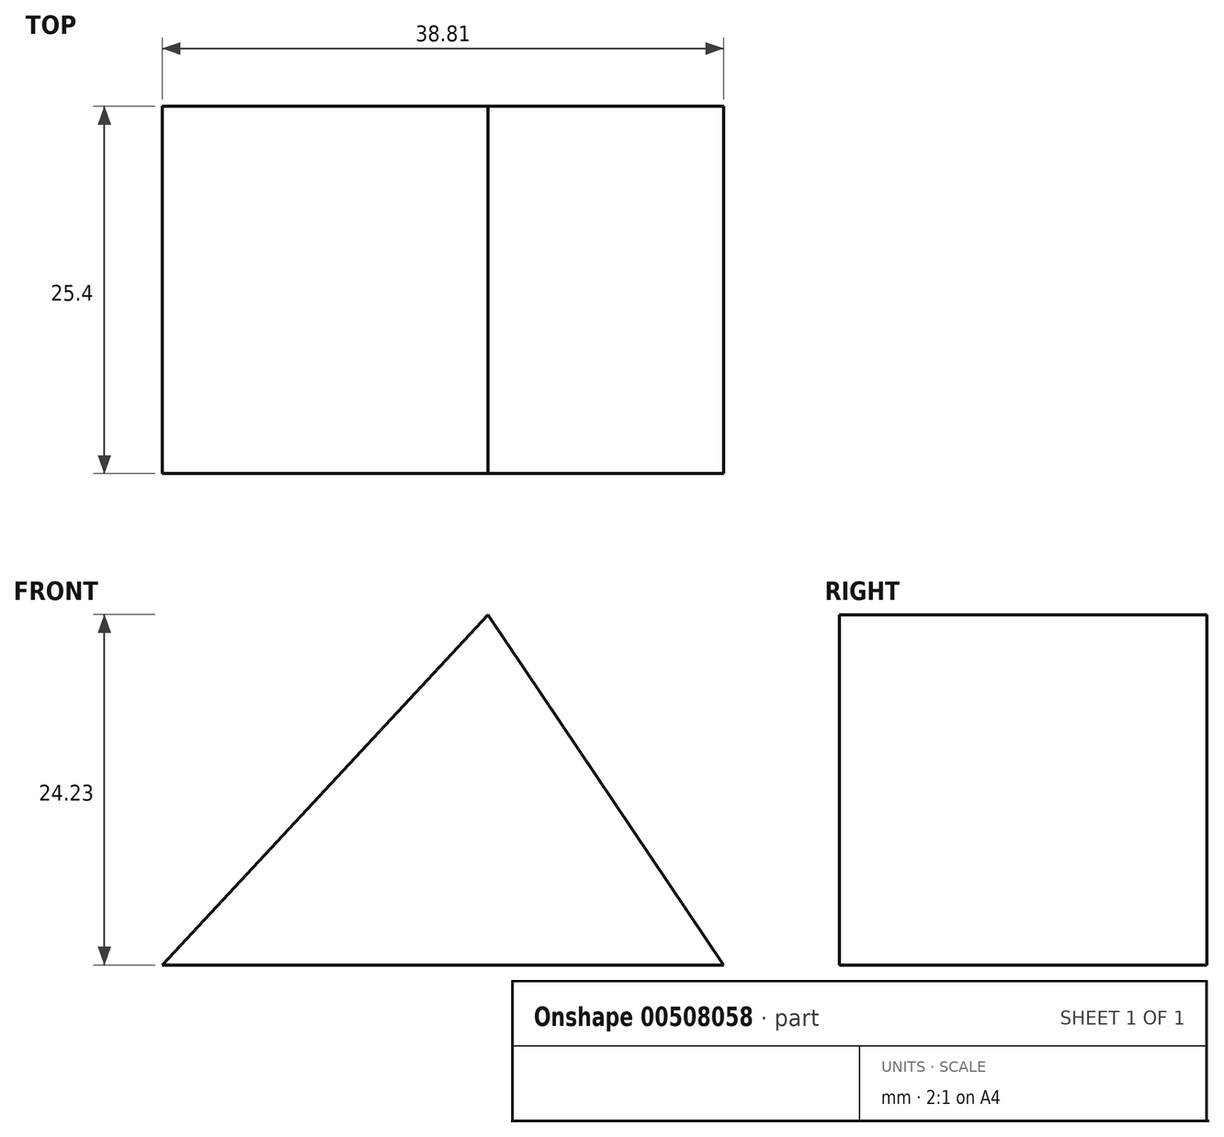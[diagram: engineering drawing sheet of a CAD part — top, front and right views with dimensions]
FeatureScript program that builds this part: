
annotation { "Feature Type Name" : "Feature", "Feature Type Description" : "" }
export const myFeature = defineFeature(function(context is Context, id is Id, definition is map)
    precondition{}
    {
        {
            var Q0;
            Q0=qCreatedBy(makeId("Front.planeOp"),FACE);
            var sketch = newSketch(context, id + "F0", { "sketchPlane" : qUnion([Q0])});
            skLineSegment(sketch, "E0", {"start": v(-45.56, 68.53) * mm, "end": v(-68.08, 44.3) * mm});
            skLineSegment(sketch, "E1", {"start": v(-68.08, 44.3) * mm, "end": v(-29.27, 44.3) * mm});
            skLineSegment(sketch, "E2", {"start": v(-29.27, 44.3) * mm, "end": v(-45.56, 68.53) * mm});
            skSolve(sketch);
        }
        {
            var Q0;
            Q0 = qSketchRegion(id + "F0", true);
            extrude(context, id + "F1", {"entities" : qUnion([Q0]), "endBound" : BoundingType.SYMMETRIC, "depth" : 25.4 * mm});
        }
    });
